# Revit family: Window_Screen-Sliding-Phantom_Screens-Prestige-Retractable_Window-04
name_source: partatom
category: Specialty Equipment
revit_build: Autodesk Revit 2017 (Build: 20181011_1645(x64)
units: mm (PartAtom-declared; Revit-internal decimal feet)

## family parameters
Always vertical = Yes
Cut with Voids When Loaded = No
OmniClass Number = 23.30.60.21
OmniClass Title = Insect Screens
Part Type = Normal
Room Calculation Point = No
Round Connector Dimension = Use Diameter
Shared = No
Work Plane-Based = No

## types (1)
- Wood Slide Bar
    Assembly Code = B2010300
    Bottom Latch Offset = 0' - 0 11/16"
    Description = Phantom retractable wood window screen
    Door Bottom Offset = 0' - 0 11/16"
    Finish = Wood-Phantom_Screens-Dark_Acacia
    Finish Screen = Screen-Insect_Mesh-Phantom_Screens-BetterVue_Mesh
    Housing Height = 0' - 2 7/32"
    Manufacturer = Phantom Mfg. (Int'l) Ltd.
    Max Height = 6' - 6"
    Max Width = 6' - 0"
    Min Width = 1' - 6"
    Model = Retractable Window Wood Veneer Application
    Not Removable Track = Yes
    Product Documentation Link = https://www.phantomscreens.com
    Product Name = Retractable Window Screen
    Product Page URL = https://www.phantomscreens.com
    Removable Track = Yes
    Removable Track Calc = No
    Slide Bar Height = 0' - 1 3/8"
    Standard Track = No
    Standard Track Calc = Yes
    Thickness = 0' - 1 29/32"
    Track Height = 0' - 1 11/32"
    Track Thickness = 0' - 0 7/8"
    Type Comments = Vertical Screen
    URL = https://www.phantomscreens.com

## geometry (parser evidence)
native form markers: Extrusion x1, Sweep x8
no freeform markers — native parametric forms only
